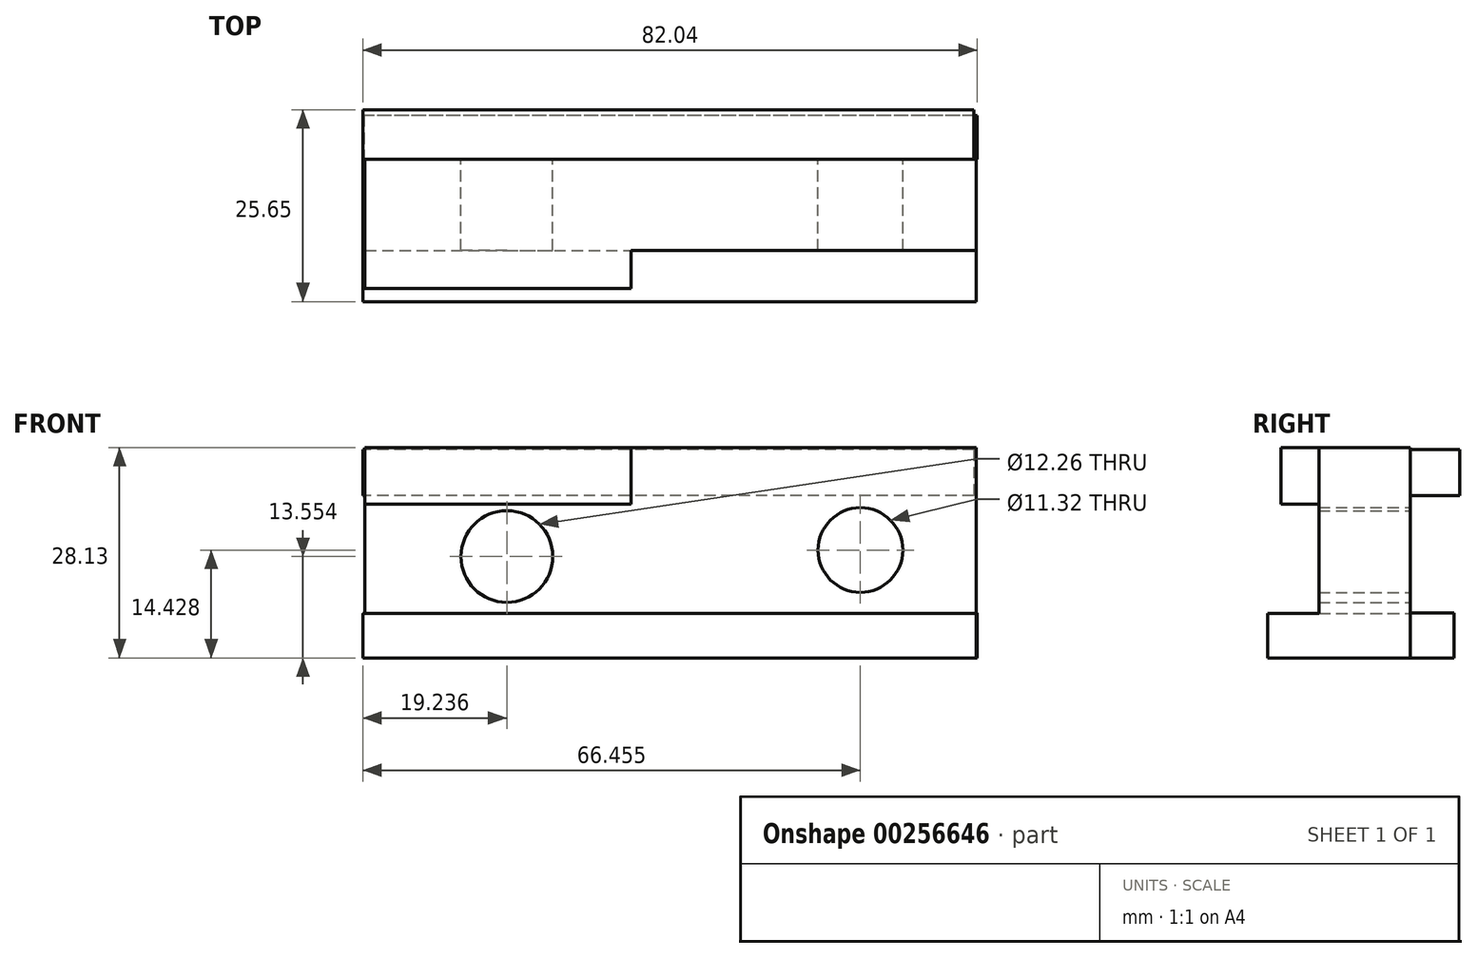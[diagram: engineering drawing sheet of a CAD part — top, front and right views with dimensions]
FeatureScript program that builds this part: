
annotation { "Feature Type Name" : "Feature", "Feature Type Description" : "" }
export const myFeature = defineFeature(function(context is Context, id is Id, definition is map)
    precondition{}
    {
        {
            var Q0;
            Q0=qCreatedBy(makeId("Front.planeOp"),FACE);
            var sketch = newSketch(context, id + "F0", { "sketchPlane" : qUnion([Q0])});
            skLineSegment(sketch, "E0.bottom", {"start": v(-35.56, 0) * mm, "end": v(46.05, 0) * mm});
            skLineSegment(sketch, "E0.top", {"start": v(-35.56, 28.13) * mm, "end": v(46.05, 28.13) * mm});
            skLineSegment(sketch, "E0.left", {"start": v(-35.56, 0) * mm, "end": v(-35.56, 28.13) * mm});
            skLineSegment(sketch, "E0.right", {"start": v(46.05, 0) * mm, "end": v(46.05, 28.13) * mm});
            skSolve(sketch);
        }
        {
            var Q0;
            Q0 = qSketchRegion(id + "F0", true);
            extrude(context, id + "F1", {"entities" : qUnion([Q0]), "depth" : 12.2 * mm});
        }
        {
            var Q0;
            Q0=qCreatedBy(makeId("Front.planeOp"),FACE);
            var sketch = newSketch(context, id + "F2", { "sketchPlane" : qUnion([Q0])});
            skLineSegment(sketch, "E1.bottom", {"start": v(46.2, 0) * mm, "end": v(-35.74, 0) * mm});
            skLineSegment(sketch, "E1.top", {"start": v(46.2, 6) * mm, "end": v(-35.74, 6) * mm});
            skLineSegment(sketch, "E1.left", {"start": v(46.2, 0) * mm, "end": v(46.2, 6) * mm});
            skLineSegment(sketch, "E1.right", {"start": v(-35.74, 0) * mm, "end": v(-35.74, 6) * mm});
            skSolve(sketch);
        }
        {
            var Q0;
            Q0 = qSketchRegion(id + "F2", true);
            extrude(context, id + "F3", {"entities" : qUnion([Q0]), "operationType" : NewBodyOperationType.ADD, "oppositeDirection" : true, "depth" : 5.84 * mm});
        }
        {
            var Q0;
            Q0=qCreatedBy(makeId("Front.planeOp"),FACE);
            var sketch = newSketch(context, id + "F4", { "sketchPlane" : qUnion([Q0])});
            skLineSegment(sketch, "E2.bottom", {"start": v(-35.85, 5.98) * mm, "end": v(46.05, 5.98) * mm});
            skLineSegment(sketch, "E2.top", {"start": v(-35.85, 0) * mm, "end": v(46.05, 0) * mm});
            skLineSegment(sketch, "E2.left", {"start": v(-35.85, 5.98) * mm, "end": v(-35.85, 0) * mm});
            skLineSegment(sketch, "E2.right", {"start": v(46.05, 5.98) * mm, "end": v(46.05, 0) * mm});
            skSolve(sketch);
        }
        {
            var Q0;
            Q0 = qSketchRegion(id + "F4", true);
            extrude(context, id + "F5", {"entities" : qUnion([Q0]), "operationType" : NewBodyOperationType.ADD, "depth" : 19.05 * mm});
        }
        {
            var Q0;
            Q0=qCreatedBy(makeId("Front.planeOp"),FACE);
            var sketch = newSketch(context, id + "F6", { "sketchPlane" : qUnion([Q0])});
            skLineSegment(sketch, "E3.bottom", {"start": v(45.76, 27.84) * mm, "end": v(-35.85, 27.84) * mm});
            skLineSegment(sketch, "E3.top", {"start": v(45.76, 21.71) * mm, "end": v(-35.85, 21.71) * mm});
            skLineSegment(sketch, "E3.left", {"start": v(45.76, 27.84) * mm, "end": v(45.76, 21.71) * mm});
            skLineSegment(sketch, "E3.right", {"start": v(-35.85, 27.84) * mm, "end": v(-35.85, 21.71) * mm});
            skSolve(sketch);
        }
        {
            var Q0;
            Q0 = qSketchRegion(id + "F6", true);
            extrude(context, id + "F7", {"entities" : qUnion([Q0]), "operationType" : NewBodyOperationType.ADD, "oppositeDirection" : true, "depth" : 6.6 * mm});
        }
        {
            var Q0;
            Q0=makeQuery(id+"F1.opExtrude","CAP_FACE",FACE,{"disambiguationData":[OSD([sQuery(id+"F0.wireOp",EDGE,"E0.bottom"),sQuery(id+"F0.wireOp",EDGE,"E0.top"),sQuery(id+"F0.wireOp",EDGE,"E0.left"),sQuery(id+"F0.wireOp",EDGE,"E0.right")])],"isStart":true});
            var sketch = newSketch(context, id + "F8", { "sketchPlane" : qUnion([Q0])});
            skCircle(sketch, "E4", {"center": v(-30.6, 14.43) * mm, "radius": 5.66 * mm});
            skCircle(sketch, "E5", {"center": v(16.61, 13.55) * mm, "radius": 6.13 * mm});
            skSolve(sketch);
        }
        {
            var Q0;
            Q0 = qSketchRegion(id + "F8", true);
            extrude(context, id + "F9", {"entities" : qUnion([Q0]), "operationType" : NewBodyOperationType.REMOVE, "oppositeDirection" : true, "depth" : 70.1 * mm});
        }
        {
            var Q0;
            Q0=makeQuery(id+"F1.opExtrude","CAP_FACE",FACE,{"disambiguationData":[OSD([sQuery(id+"F0.wireOp",EDGE,"E0.bottom"),sQuery(id+"F0.wireOp",EDGE,"E0.top"),sQuery(id+"F0.wireOp",EDGE,"E0.left"),sQuery(id+"F0.wireOp",EDGE,"E0.right")])],"isStart":false});
            var sketch = newSketch(context, id + "F10", { "sketchPlane" : qUnion([Q0])});
            skLineSegment(sketch, "E6.bottom", {"start": v(-35.56, 20.55) * mm, "end": v(0, 20.55) * mm});
            skLineSegment(sketch, "E6.top", {"start": v(-35.56, 28.13) * mm, "end": v(0, 28.13) * mm});
            skLineSegment(sketch, "E6.left", {"start": v(-35.56, 20.55) * mm, "end": v(-35.56, 28.13) * mm});
            skLineSegment(sketch, "E6.right", {"start": v(0, 20.55) * mm, "end": v(0, 28.13) * mm});
            skSolve(sketch);
        }
        {
            var Q0;
            Q0 = qSketchRegion(id + "F10", true);
            extrude(context, id + "F11", {"entities" : qUnion([Q0]), "operationType" : NewBodyOperationType.ADD, "depth" : 5.08 * mm});
        }
    });
